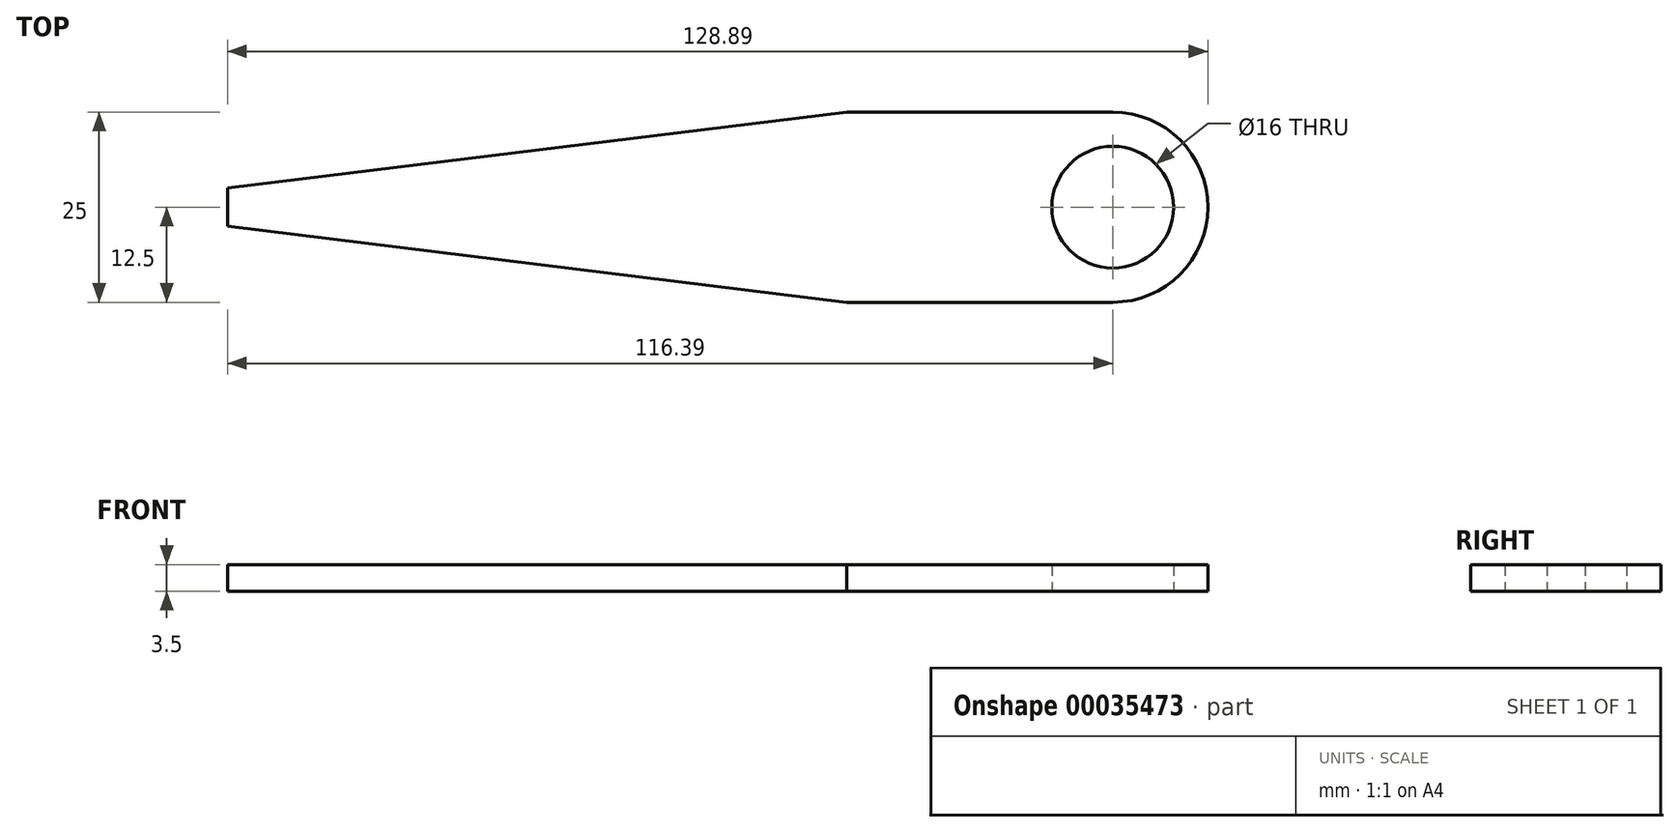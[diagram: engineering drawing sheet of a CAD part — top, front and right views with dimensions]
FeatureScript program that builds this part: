
annotation { "Feature Type Name" : "Feature", "Feature Type Description" : "" }
export const myFeature = defineFeature(function(context is Context, id is Id, definition is map)
    precondition{}
    {
        {
            var Q0;
            Q0=qCreatedBy(makeId("Top.planeOp"),FACE);
            var sketch = newSketch(context, id + "F0", { "sketchPlane" : qUnion([Q0])});
            skCircle(sketch, "E0", {"center": v(0, 0) * mm, "radius": 8 * mm});
            skCircle(sketch, "E1", {"center": v(0, 0) * mm, "radius": 12.5 * mm});
            skLineSegment(sketch, "E2", {"start": v(-35, 12.5) * mm, "end": v(0, 12.5) * mm});
            skLineSegment(sketch, "E3", {"start": v(-35, -12.5) * mm, "end": v(0, -12.5) * mm});
            skLineSegment(sketch, "E4", {"start": v(-35, 12.5) * mm, "end": v(-115.26, 12.5) * mm, "construction": true});
            skLineSegment(sketch, "E5", {"start": v(-35, 12.5) * mm, "end": v(-116.39, 2.5) * mm});
            skLineSegment(sketch, "E6", {"start": v(-35, -12.5) * mm, "end": v(-114.55, -12.5) * mm, "construction": true});
            skLineSegment(sketch, "E7", {"start": v(-35, -12.5) * mm, "end": v(-116.39, -2.5) * mm});
            skLineSegment(sketch, "E8", {"start": v(-116.39, 2.5) * mm, "end": v(-116.39, -2.5) * mm});
            skSolve(sketch);
        }
        {
            var Q0;
            Q0 = qSketchRegion(id + "F0", true);
            extrude(context, id + "F1", {"entities" : qUnion([Q0]), "depth" : 3.5 * mm});
        }
        {
            var Q0;
            Q0=qCreatedBy(makeId("Top.planeOp"),FACE);
            var sketch = newSketch(context, id + "F2", { "sketchPlane" : qUnion([Q0])});
            skCircle(sketch, "E9", {"center": v(0, 0) * mm, "radius": 12.5 * mm});
            skCircle(sketch, "E10.0", {"center": v(0, 0) * mm, "radius": 17.5 * mm});
            skLineSegment(sketch, "E11.bottom", {"start": v(-116.47, 1.67) * mm, "end": v(-96.47, 1.67) * mm});
            skLineSegment(sketch, "E11.top", {"start": v(-116.47, -1) * mm, "end": v(-96.47, -1) * mm});
            skLineSegment(sketch, "E11.left", {"start": v(-116.47, 1.67) * mm, "end": v(-116.47, -1) * mm});
            skLineSegment(sketch, "E11.right", {"start": v(-96.47, 1.67) * mm, "end": v(-96.47, -1) * mm});
            skSolve(sketch);
        }
        {
            var Q0;
            Q0=makeQuery(id+"F2.imprint","IMPRINT",FACE,{"disambiguationData":[TD([[makeQuery(id+"F2.imprint","IMPRINT",EDGE,{"derivedFrom":sQuery(id+"F2.wireOp",EDGE,"E11.bottom")}),-1.0]])]});
            var Q1;
            Q1=makeQuery(id+"F2.imprint","IMPRINT",FACE,{"disambiguationData":[TD([[makeQuery(id+"F2.imprint","IMPRINT",EDGE,{"derivedFrom":sQuery(id+"F2.wireOp",EDGE,"E9")}),-1.0]])]});
            extrude(context, id + "F3", {"entities" : qUnion([Q0, Q1]), "operationType" : NewBodyOperationType.REMOVE, "oppositeDirection" : true, "depth" : 2 * mm});
        }
    });
